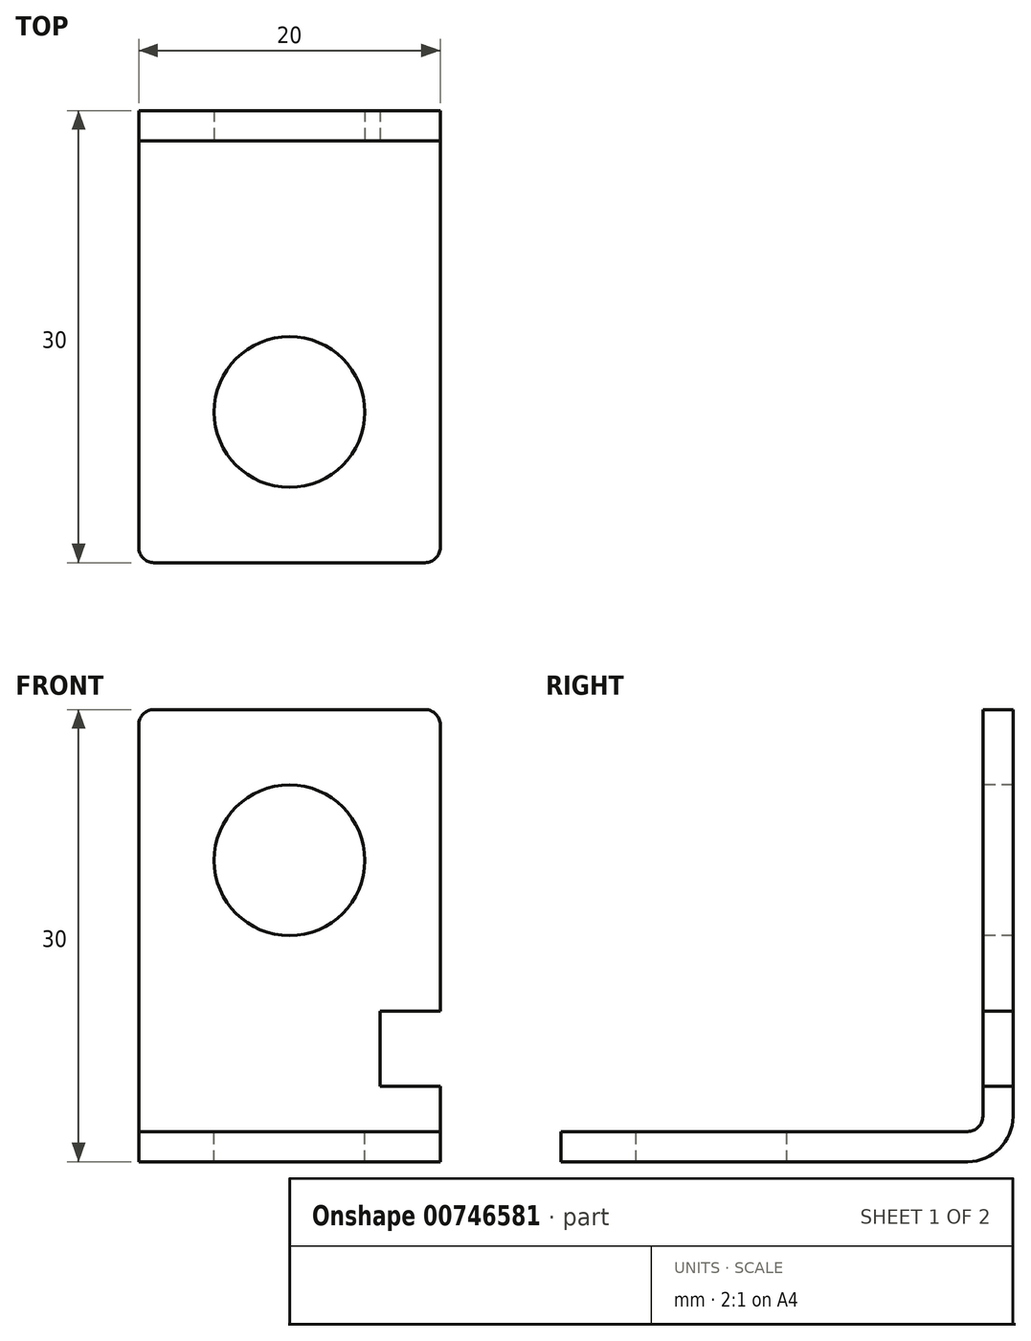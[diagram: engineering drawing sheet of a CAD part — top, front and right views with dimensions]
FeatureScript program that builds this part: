
annotation { "Feature Type Name" : "Feature", "Feature Type Description" : "" }
export const myFeature = defineFeature(function(context is Context, id is Id, definition is map)
    precondition{}
    {
        {
            var Q0;
            Q0=qCreatedBy(makeId("Top.planeOp"),FACE);
            var sketch = newSketch(context, id + "F0", { "sketchPlane" : qUnion([Q0])});
            skLineSegment(sketch, "E0.bottom", {"start": v(-10, 15) * mm, "end": v(10, 15) * mm});
            skLineSegment(sketch, "E0.top", {"start": v(-10, -15) * mm, "end": v(10, -15) * mm});
            skLineSegment(sketch, "E0.left", {"start": v(-10, 15) * mm, "end": v(-10, -15) * mm});
            skLineSegment(sketch, "E0.right", {"start": v(10, 15) * mm, "end": v(10, -15) * mm});
            skPoint(sketch, "E0.middle", {"position": v(0, 0) * mm});
            skSolve(sketch);
        }
        {
            var Q0;
            Q0 = qSketchRegion(id + "F0", true);
            extrude(context, id + "F1", {"entities" : qUnion([Q0]), "depth" : 2 * mm, "offsetDistance" : 25 * mm});
        }
        {
            var Q0;
            Q0=makeQuery(id+"F1.opExtrude","SWEPT_FACE",FACE,{"disambiguationData":[OSD([sQuery(id+"F0.wireOp",EDGE,"E0.bottom")])]});
            var sketch = newSketch(context, id + "F2", { "sketchPlane" : qUnion([Q0])});
            skLineSegment(sketch, "E1.bottom", {"start": v(-10, 0) * mm, "end": v(10, 0) * mm});
            skLineSegment(sketch, "E1.top", {"start": v(-10, 30) * mm, "end": v(10, 30) * mm});
            skLineSegment(sketch, "E1.left", {"start": v(-10, 0) * mm, "end": v(-10, 30) * mm});
            skLineSegment(sketch, "E1.right", {"start": v(10, 0) * mm, "end": v(10, 30) * mm});
            skSolve(sketch);
        }
        {
            var Q0;
            Q0 = qSketchRegion(id + "F2", true);
            extrude(context, id + "F3", {"entities" : qUnion([Q0]), "operationType" : NewBodyOperationType.ADD, "oppositeDirection" : true, "depth" : 2 * mm, "offsetDistance" : 25 * mm});
        }
        {
            var Q0;
            Q0=makeQuery(id+"F3.opExtrude","CAP_FACE",FACE,{"disambiguationData":[OSD([sQuery(id+"F2.wireOp",EDGE,"E1.bottom"),sQuery(id+"F2.wireOp",EDGE,"E1.top"),sQuery(id+"F2.wireOp",EDGE,"E1.left"),sQuery(id+"F2.wireOp",EDGE,"E1.right")])],"isStart":false});
            var sketch = newSketch(context, id + "F4", { "sketchPlane" : qUnion([Q0])});
            skLineSegment(sketch, "E2.bottom", {"start": v(10, 10) * mm, "end": v(6, 10) * mm});
            skLineSegment(sketch, "E2.top", {"start": v(10, 5) * mm, "end": v(6, 5) * mm});
            skLineSegment(sketch, "E2.left", {"start": v(10, 10) * mm, "end": v(10, 5) * mm});
            skLineSegment(sketch, "E2.right", {"start": v(6, 10) * mm, "end": v(6, 5) * mm});
            skCircle(sketch, "E3", {"center": v(0, 20) * mm, "radius": 5 * mm});
            skSolve(sketch);
        }
        {
            var Q0;
            Q0 = qSketchRegion(id + "F4", true);
            extrude(context, id + "F5", {"entities" : qUnion([Q0]), "operationType" : NewBodyOperationType.REMOVE, "endBound" : BoundingType.THROUGH_ALL, "oppositeDirection" : true, "depth" : 25 * mm, "offsetDistance" : 25 * mm});
        }
        {
            var Q0;
            Q0=makeQuery(id+"F1.opExtrude","CAP_FACE",FACE,{"disambiguationData":[OSD([sQuery(id+"F0.wireOp",EDGE,"E0.bottom"),sQuery(id+"F0.wireOp",EDGE,"E0.top"),sQuery(id+"F0.wireOp",EDGE,"E0.left"),sQuery(id+"F0.wireOp",EDGE,"E0.right")])],"isStart":false});
            var sketch = newSketch(context, id + "F6", { "sketchPlane" : qUnion([Q0])});
            skCircle(sketch, "E4", {"center": v(0, -5) * mm, "radius": 5 * mm});
            skSolve(sketch);
        }
        {
            var Q0;
            Q0 = qSketchRegion(id + "F6", true);
            extrude(context, id + "F7", {"entities" : qUnion([Q0]), "operationType" : NewBodyOperationType.REMOVE, "endBound" : BoundingType.THROUGH_ALL, "oppositeDirection" : true, "depth" : 25 * mm, "offsetDistance" : 25 * mm});
        }
        {
            var Q0;
            Q0=makeQuery(id+"F1.opExtrude","SWEPT_EDGE",EDGE,{"disambiguationData":[OSD([sQuery(id+"F0.wireOp",EDGE,"E0.top"),sQuery(id+"F0.wireOp",EDGE,"E0.left")])]});
            var Q1;
            Q1=makeQuery(id+"F1.opExtrude","SWEPT_EDGE",EDGE,{"disambiguationData":[OSD([sQuery(id+"F0.wireOp",EDGE,"E0.top"),sQuery(id+"F0.wireOp",EDGE,"E0.right")])]});
            var Q2;
            Q2=makeQuery(id+"F3.opExtrude","SWEPT_EDGE",EDGE,{"disambiguationData":[OSD([sQuery(id+"F2.wireOp",EDGE,"E1.top"),sQuery(id+"F2.wireOp",EDGE,"E1.left")])]});
            var Q3;
            Q3=makeQuery(id+"F3.opExtrude","SWEPT_EDGE",EDGE,{"disambiguationData":[OSD([sQuery(id+"F2.wireOp",EDGE,"E1.top"),sQuery(id+"F2.wireOp",EDGE,"E1.right")])]});
            var Q4;
            Q4=makeQuery(id+"F3.boolean.opBoolean","INTERSECT",EDGE,{"derivedFrom":[makeQuery(id+"F1.opExtrude","CAP_FACE",FACE,{"disambiguationData":[OSD([sQuery(id+"F0.wireOp",EDGE,"E0.bottom"),sQuery(id+"F0.wireOp",EDGE,"E0.top"),sQuery(id+"F0.wireOp",EDGE,"E0.left"),sQuery(id+"F0.wireOp",EDGE,"E0.right")])],"isStart":false}),makeQuery(id+"F3.opExtrude","CAP_FACE",FACE,{"disambiguationData":[OSD([sQuery(id+"F2.wireOp",EDGE,"E1.bottom"),sQuery(id+"F2.wireOp",EDGE,"E1.top"),sQuery(id+"F2.wireOp",EDGE,"E1.left"),sQuery(id+"F2.wireOp",EDGE,"E1.right")])],"isStart":false})]});
            fillet(context, id + "F8", {"entities" : qUnion([Q0, Q1, Q2, Q3, Q4]), "radius" : 1 * mm, "tangentPropagation" : true, "allowEdgeOverflow" : false});
        }
        {
            var Q0;
            Q0=makeQuery(id+"F1.opExtrude","CAP_EDGE",EDGE,{"disambiguationData":[OSD([sQuery(id+"F0.wireOp",EDGE,"E0.bottom")])],"isStart":true});
            fillet(context, id + "F9", {"entities" : qUnion([Q0]), "radius" : 3 * mm, "tangentPropagation" : true, "allowEdgeOverflow" : false});
        }
    });
